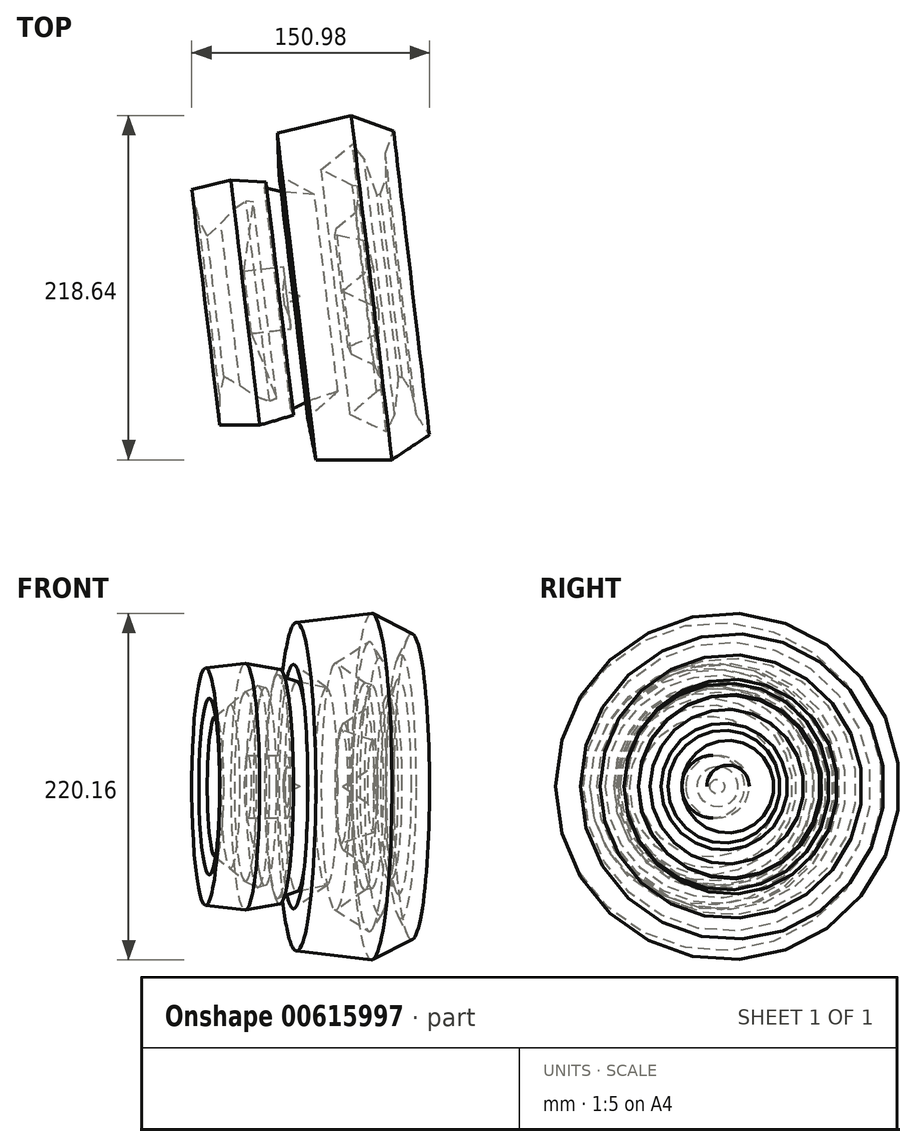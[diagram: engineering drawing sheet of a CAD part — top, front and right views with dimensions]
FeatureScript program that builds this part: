
annotation { "Feature Type Name" : "Feature", "Feature Type Description" : "" }
export const myFeature = defineFeature(function(context is Context, id is Id, definition is map)
    precondition{}
    {
        {
            var Q0;
            Q0=qCreatedBy(makeId("Top.planeOp"),FACE);
            var sketch = newSketch(context, id + "F0", { "sketchPlane" : qUnion([Q0])});
            skLineSegment(sketch, "E0", {"start": v(-30.5, -21.22) * mm, "end": v(-46.4, 20.12) * mm});
            skLineSegment(sketch, "E1", {"start": v(-46.4, 20.12) * mm, "end": v(-21.46, 23.05) * mm});
            skLineSegment(sketch, "E2", {"start": v(-21.46, 23.05) * mm, "end": v(-22.28, 30.03) * mm});
            skLineSegment(sketch, "E3", {"start": v(-22.28, 30.03) * mm, "end": v(-25.37, 37.97) * mm});
            skLineSegment(sketch, "E4", {"start": v(-25.37, 37.97) * mm, "end": v(-15.6, 43.84) * mm});
            skLineSegment(sketch, "E5", {"start": v(-15.6, 43.84) * mm, "end": v(11.31, 47.02) * mm});
            skLineSegment(sketch, "E6", {"start": v(11.31, 47.02) * mm, "end": v(34.06, 36.01) * mm});
            skLineSegment(sketch, "E7", {"start": v(34.06, 36.01) * mm, "end": v(34.06, 20.12) * mm});
            skLineSegment(sketch, "E8", {"start": v(34.06, 20.12) * mm, "end": v(14.98, 11.31) * mm});
            skLineSegment(sketch, "E9", {"start": v(14.98, 11.31) * mm, "end": v(16.96, 7.03) * mm});
            skLineSegment(sketch, "E10", {"start": v(16.96, 7.03) * mm, "end": v(31.61, 0) * mm});
            skLineSegment(sketch, "E11", {"start": v(31.61, 0) * mm, "end": v(37.48, -14.86) * mm});
            skLineSegment(sketch, "E12", {"start": v(37.48, -14.86) * mm, "end": v(33.1, -16.6) * mm});
            skLineSegment(sketch, "E13", {"start": v(33.1, -16.6) * mm, "end": v(16.2, -31.24) * mm});
            skLineSegment(sketch, "E14", {"start": v(16.2, -31.24) * mm, "end": v(39.2, -42.25) * mm});
            skLineSegment(sketch, "E15", {"start": v(39.2, -42.25) * mm, "end": v(44.44, -31.29) * mm});
            skLineSegment(sketch, "E16", {"start": v(44.44, -31.29) * mm, "end": v(46.77, -7.28) * mm});
            skLineSegment(sketch, "E17", {"start": v(46.77, -7.28) * mm, "end": v(49.27, -7.52) * mm});
            skLineSegment(sketch, "E18", {"start": v(49.27, -7.52) * mm, "end": v(55.09, -16.6) * mm});
            skLineSegment(sketch, "E19", {"start": v(55.09, -16.6) * mm, "end": v(58.27, -31.73) * mm});
            skLineSegment(sketch, "E20", {"start": v(58.27, -31.73) * mm, "end": v(66.58, -44.2) * mm});
            skLineSegment(sketch, "E21", {"start": v(66.58, -44.2) * mm, "end": v(42.7, -60.12) * mm});
            skLineSegment(sketch, "E22", {"start": v(42.7, -60.12) * mm, "end": v(15.96, -60.12) * mm});
            skLineSegment(sketch, "E23", {"start": v(15.96, -60.12) * mm, "end": v(-5.56, -60.12) * mm});
            skLineSegment(sketch, "E24", {"start": v(-5.56, -60.12) * mm, "end": v(-10.7, -33.69) * mm});
            skLineSegment(sketch, "E25", {"start": v(-10.7, -33.69) * mm, "end": v(8.38, -16.6) * mm});
            skLineSegment(sketch, "E26", {"start": v(8.38, -16.6) * mm, "end": v(-9.97, -22.68) * mm});
            skLineSegment(sketch, "E27", {"start": v(-9.97, -22.68) * mm, "end": v(-21.46, -28.3) * mm});
            skLineSegment(sketch, "E28", {"start": v(-21.46, -28.3) * mm, "end": v(-19.79, -31.73) * mm});
            skLineSegment(sketch, "E29", {"start": v(-19.79, -31.73) * mm, "end": v(-41.27, -38.1) * mm});
            skLineSegment(sketch, "E30", {"start": v(-41.27, -38.1) * mm, "end": v(-66.7, -38.1) * mm});
            skLineSegment(sketch, "E31", {"start": v(-66.7, -38.1) * mm, "end": v(-66.7, -18.77) * mm});
            skLineSegment(sketch, "E32", {"start": v(-66.7, -18.77) * mm, "end": v(-64.01, -7.03) * mm});
            skLineSegment(sketch, "E33", {"start": v(-64.01, -7.03) * mm, "end": v(-53.74, -12.9) * mm});
            skLineSegment(sketch, "E34", {"start": v(-53.74, -12.9) * mm, "end": v(-43.23, -20) * mm});
            skLineSegment(sketch, "E35", {"start": v(-43.23, -20) * mm, "end": v(-34.91, -22.93) * mm});
            skLineSegment(sketch, "E36", {"start": v(-34.91, -22.93) * mm, "end": v(-30.5, -21.22) * mm});
            skSolve(sketch);
        }
        {
            var Q0;
            Q0=makeQuery(id+"F0.imprint","IMPRINT",FACE,{"disambiguationData":[TD([[makeQuery(id+"F0.imprint","IMPRINT",EDGE,{"derivedFrom":sQuery(id+"F0.wireOp",EDGE,"E0")}),-1.0]])]});
            var Q1;
            Q1=sQuery(id+"F0.wireOp",EDGE,"E5");
            revolve(context, id + "F1", {"entities" : qUnion([Q0]), "axis" : qUnion([Q1]), "revolveType" : RevolveType.FULL});
        }
    });
